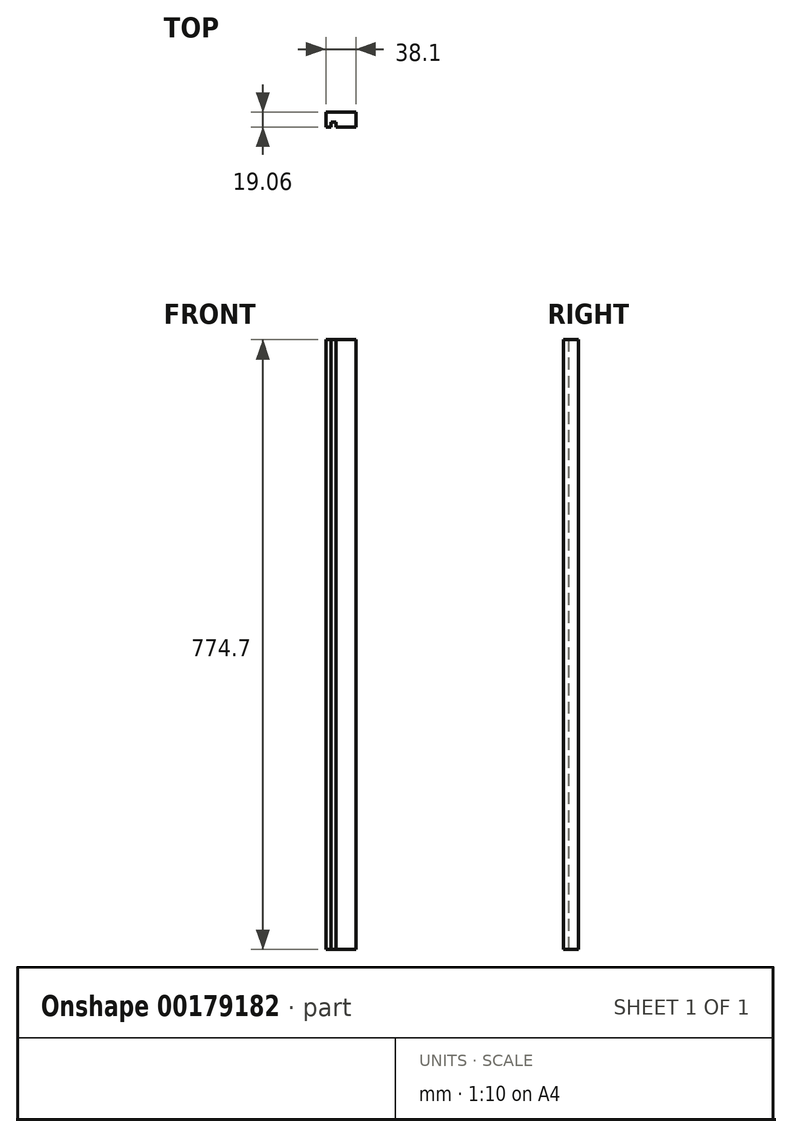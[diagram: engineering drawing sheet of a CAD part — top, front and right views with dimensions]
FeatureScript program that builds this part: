
annotation { "Feature Type Name" : "Feature", "Feature Type Description" : "" }
export const myFeature = defineFeature(function(context is Context, id is Id, definition is map)
    precondition{}
    {
        {
            var Q0;
            Q0=qCreatedBy(makeId("Front.planeOp"),FACE);
            var sketch = newSketch(context, id + "F0", { "sketchPlane" : qUnion([Q0])});
            skLineSegment(sketch, "E0.bottom", {"start": v(-32, 387.35) * mm, "end": v(6.1, 387.35) * mm});
            skLineSegment(sketch, "E0.top", {"start": v(-32, -387.35) * mm, "end": v(6.1, -387.35) * mm});
            skLineSegment(sketch, "E0.left", {"start": v(-32, 387.35) * mm, "end": v(-32, -387.35) * mm});
            skLineSegment(sketch, "E0.right", {"start": v(6.1, 387.35) * mm, "end": v(6.1, -387.35) * mm});
            skLineSegment(sketch, "E1", {"start": v(-32, 0) * mm, "end": v(6.1, 0) * mm});
            skSolve(sketch);
        }
        {
            var Q0;
            {var subQ0=sQuery(id+"F0.wireOp",EDGE,"E0.bottom");Q0=makeQuery(id+"F0.imprint","IMPRINT",FACE,{"disambiguationData":[TD([[makeQuery(id+"F0.imprint","IMPRINT",EDGE,{"derivedFrom":subQ0}),-1.0]])]});}
            var Q1;
            {var subQ0=sQuery(id+"F0.wireOp",EDGE,"E0.top");Q1=makeQuery(id+"F0.imprint","IMPRINT",FACE,{"disambiguationData":[TD([[makeQuery(id+"F0.imprint","IMPRINT",EDGE,{"derivedFrom":subQ0}),1.0]])]});}
            extrude(context, id + "F1", {"entities" : qUnion([Q0, Q1]), "depth" : 19.05 * mm, "symmetric" : true});
        }
        {
            var Q0;
            Q0=makeQuery(id+"F1.opExtrude","CAP_FACE",FACE,{"disambiguationData":[OSD([sQuery(id+"F0.wireOp",EDGE,"E0.bottom"),sQuery(id+"F0.wireOp",EDGE,"E0.top"),sQuery(id+"F0.wireOp",EDGE,"E0.left"),sQuery(id+"F0.wireOp",EDGE,"E0.right")])],"isStart":false});
            var sketch = newSketch(context, id + "F2", { "sketchPlane" : qUnion([Q0])});
            skLineSegment(sketch, "E2.bottom", {"start": v(-25.65, 387.35) * mm, "end": v(-19.3, 387.35) * mm});
            skLineSegment(sketch, "E2.top", {"start": v(-25.65, -387.35) * mm, "end": v(-19.3, -387.35) * mm});
            skLineSegment(sketch, "E2.left", {"start": v(-25.65, 387.35) * mm, "end": v(-25.65, -387.35) * mm});
            skLineSegment(sketch, "E2.right", {"start": v(-19.3, 387.35) * mm, "end": v(-19.3, -387.35) * mm});
            skSolve(sketch);
        }
        {
            var Q0;
            Q0=makeQuery(id+"F2.imprint","IMPRINT",FACE,{"disambiguationData":[TD([[makeQuery(id+"F2.imprint","IMPRINT",EDGE,{"derivedFrom":sQuery(id+"F2.wireOp",EDGE,"E2.bottom")}),-1.0]])]});
            extrude(context, id + "F3", {"entities" : qUnion([Q0]), "operationType" : NewBodyOperationType.REMOVE, "oppositeDirection" : true, "depth" : 6.35 * mm});
        }
    });
